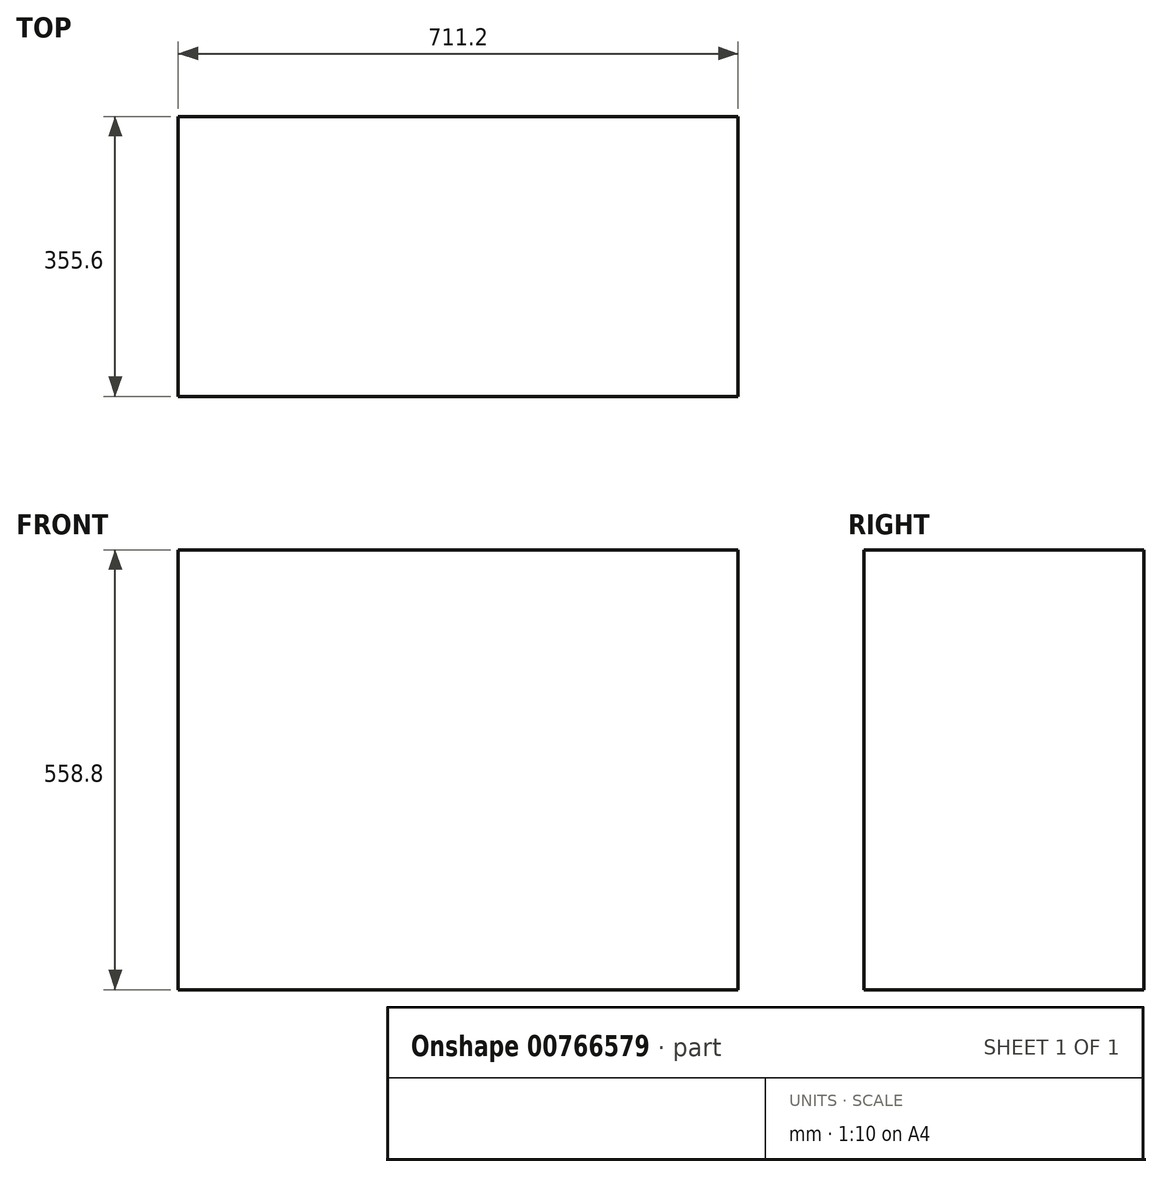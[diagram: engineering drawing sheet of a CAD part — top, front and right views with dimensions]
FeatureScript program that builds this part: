
annotation { "Feature Type Name" : "Feature", "Feature Type Description" : "" }
export const myFeature = defineFeature(function(context is Context, id is Id, definition is map)
    precondition{}
    {
        {
            var Q0;
            Q0=qCreatedBy(makeId("Top.planeOp"),FACE);
            var sketch = newSketch(context, id + "F0", { "sketchPlane" : qUnion([Q0])});
            skLineSegment(sketch, "E0.bottom", {"start": v(-355.6, 177.8) * mm, "end": v(355.6, 177.8) * mm});
            skLineSegment(sketch, "E0.top", {"start": v(-355.6, -177.8) * mm, "end": v(355.6, -177.8) * mm});
            skLineSegment(sketch, "E0.left", {"start": v(-355.6, 177.8) * mm, "end": v(-355.6, -177.8) * mm});
            skLineSegment(sketch, "E0.right", {"start": v(355.6, 177.8) * mm, "end": v(355.6, -177.8) * mm});
            skLineSegment(sketch, "E1", {"start": v(-355.6, 177.8) * mm, "end": v(355.6, -177.8) * mm, "construction": true});
            skSolve(sketch);
        }
        {
            var Q0;
            Q0=qSketchRegion(id+"F0",true);
            extrude(context, id + "F1", {"entities" : qUnion([Q0]), "depth" : 558.8 * mm, "offsetDistance" : 25.4 * mm});
        }
    });
